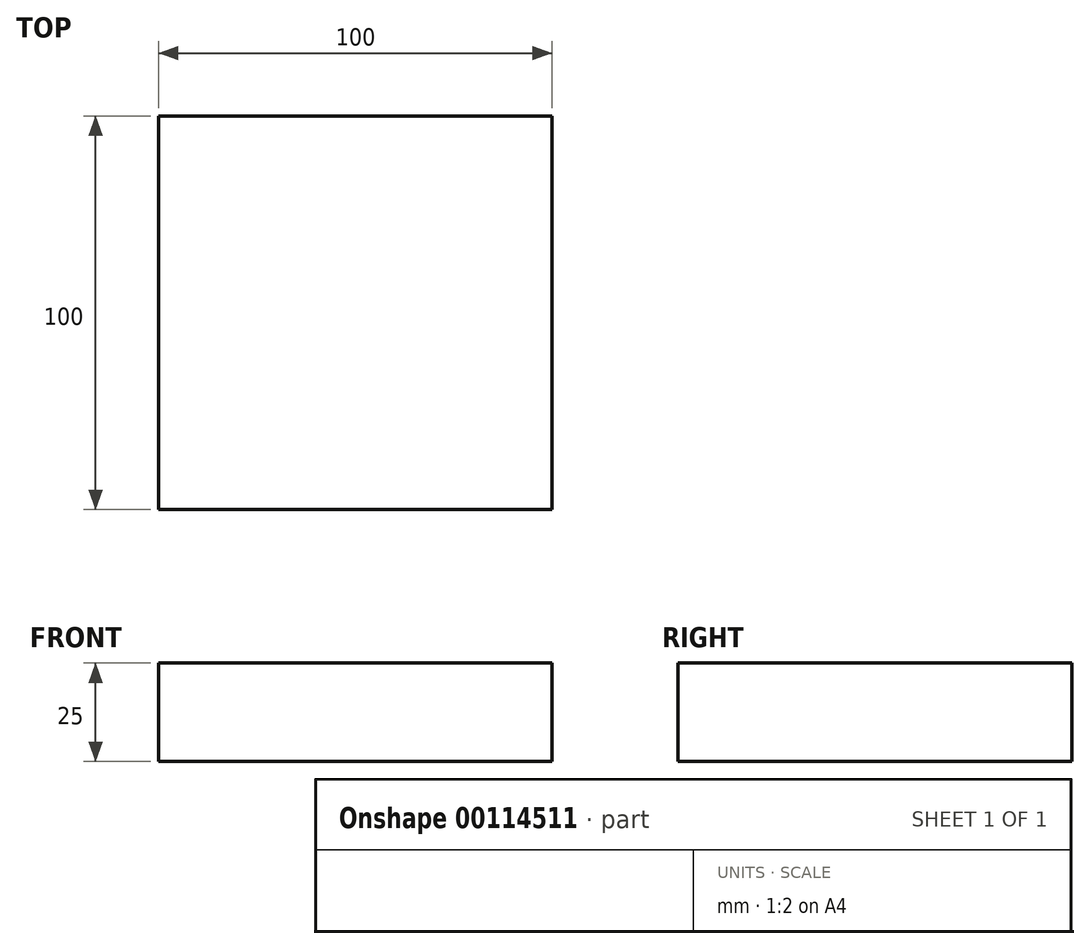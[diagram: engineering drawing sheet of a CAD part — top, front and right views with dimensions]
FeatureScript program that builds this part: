
annotation { "Feature Type Name" : "Feature", "Feature Type Description" : "" }
export const myFeature = defineFeature(function(context is Context, id is Id, definition is map)
    precondition{}
    {
        {
            var Q0;
            Q0=qCreatedBy(makeId("Top.planeOp"),FACE);
            var sketch = newSketch(context, id + "F0", { "sketchPlane" : qUnion([Q0])});
            skLineSegment(sketch, "E0.bottom", {"start": v(50, -50) * mm, "end": v(-50, -50) * mm});
            skLineSegment(sketch, "E0.top", {"start": v(50, 50) * mm, "end": v(-50, 50) * mm});
            skLineSegment(sketch, "E0.left", {"start": v(50, -50) * mm, "end": v(50, 50) * mm});
            skLineSegment(sketch, "E0.right", {"start": v(-50, -50) * mm, "end": v(-50, 50) * mm});
            skPoint(sketch, "E0.middle", {"position": v(0, 0) * mm});
            skSolve(sketch);
        }
        {
            var Q0;
            Q0 = qSketchRegion(id + "F0", true);
            extrude(context, id + "F1", {"entities" : qUnion([Q0]), "depth" : 25 * mm});
        }
    });
